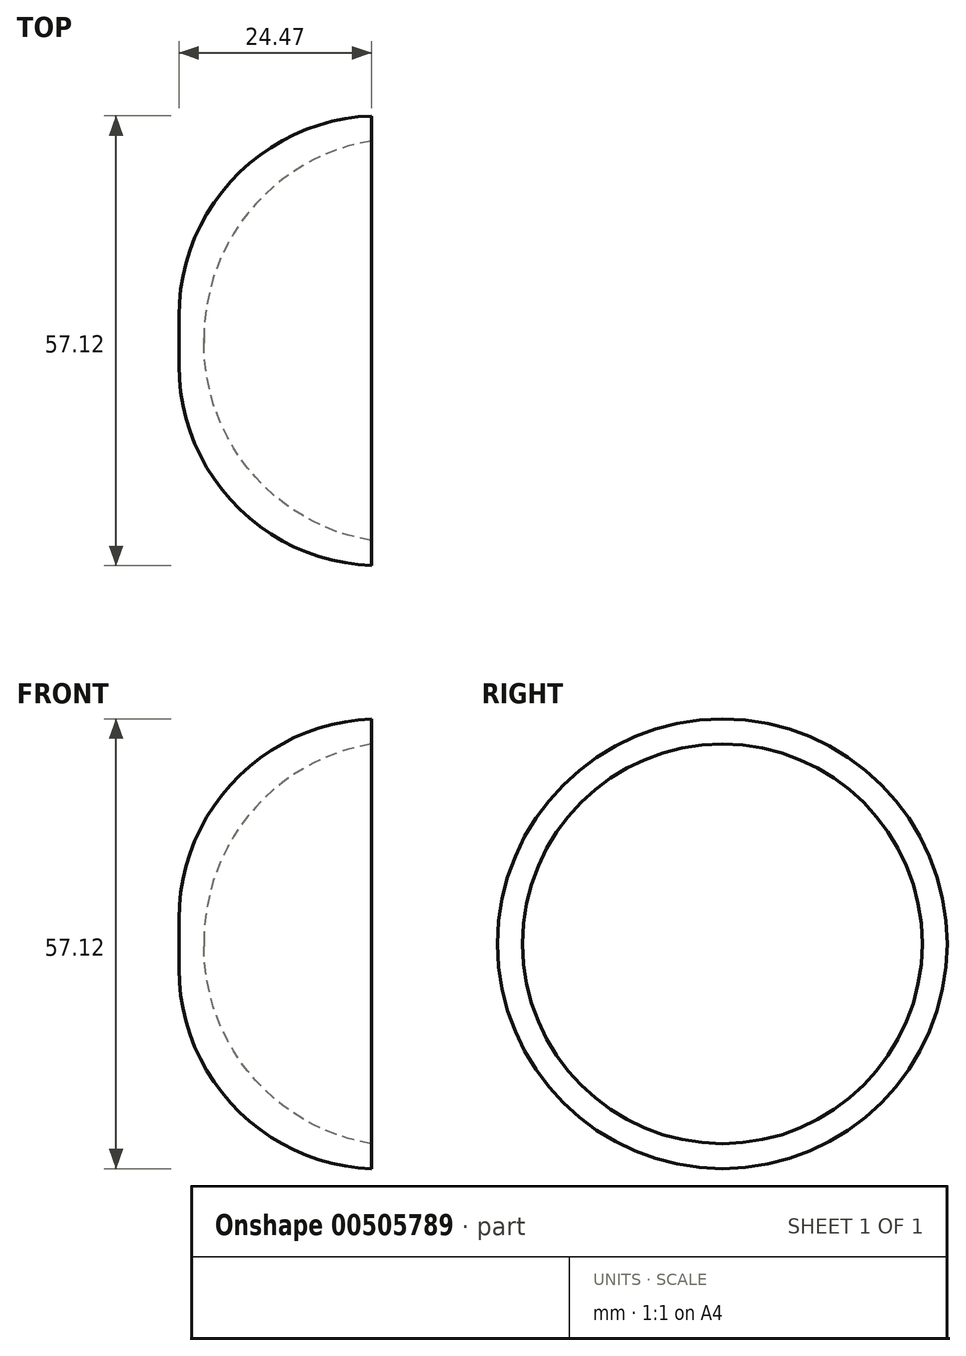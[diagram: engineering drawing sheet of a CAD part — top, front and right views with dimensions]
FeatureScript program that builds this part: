
annotation { "Feature Type Name" : "Feature", "Feature Type Description" : "" }
export const myFeature = defineFeature(function(context is Context, id is Id, definition is map)
    precondition{}
    {
        {
            var Q0;
            Q0=qCreatedBy(makeId("Front.planeOp"),FACE);
            var sketch = newSketch(context, id + "F0", { "sketchPlane" : qUnion([Q0])});
            skLineSegment(sketch, "E0", {"start": v(0, 0) * mm, "end": v(0, 3.18) * mm});
            skLineSegment(sketch, "E1", {"start": v(0, 0) * mm, "end": v(3.18, 0) * mm});
            skArc(sketch, "E2", {"start": v(24.47, 28.56) * mm, "mid": v(7.11, 20.8) * mm, "end": v(0, 3.17) * mm});
            skLineSegment(sketch, "E3", {"start": v(24.47, 25.38) * mm, "end": v(24.47, 28.56) * mm});
            skLineSegment(sketch, "E4", {"start": v(3.18, 0) * mm, "end": v(3.18, 0.32) * mm});
            skArc(sketch, "E5", {"start": v(24.47, 25.38) * mm, "mid": v(9.22, 16.76) * mm, "end": v(3.18, 0.32) * mm});
            skSolve(sketch);
        }
        {
            var Q0;
            Q0=makeQuery(id+"F0.imprint","IMPRINT",FACE,{"disambiguationData":[TD([[makeQuery(id+"F0.imprint","IMPRINT",EDGE,{"derivedFrom":sQuery(id+"F0.wireOp",EDGE,"E0")}),-1.0]])]});
            var Q1;
            Q1=sQuery(id+"F0.wireOp",EDGE,"E1");
            revolve(context, id + "F1", {"entities" : qUnion([Q0]), "axis" : qUnion([Q1]), "revolveType" : RevolveType.FULL});
        }
    });
